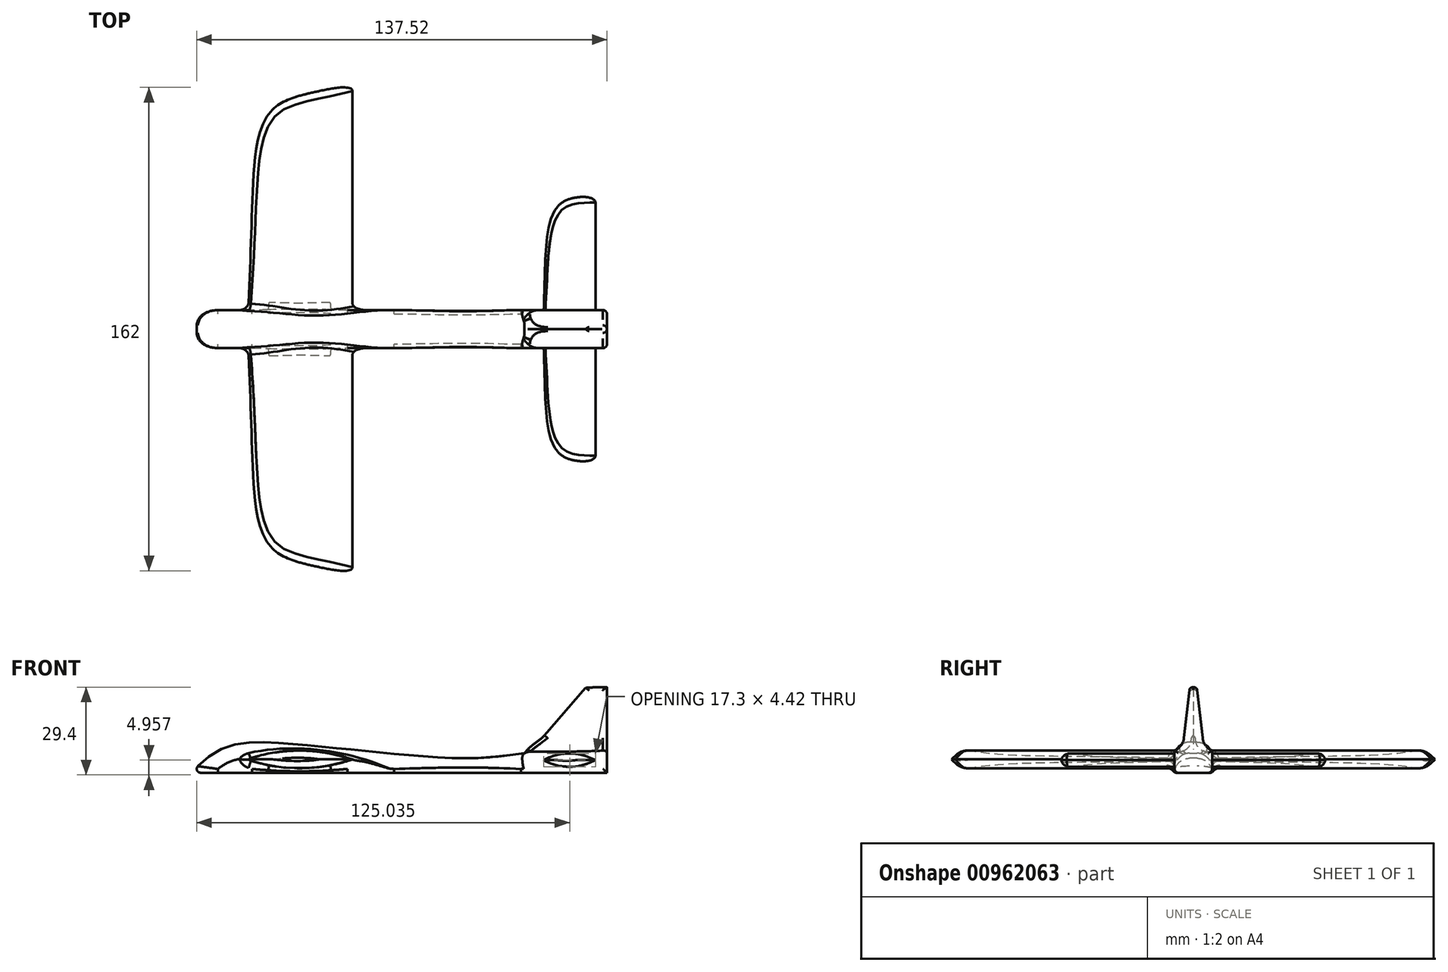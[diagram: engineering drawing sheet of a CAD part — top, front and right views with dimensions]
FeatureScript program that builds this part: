
annotation { "Feature Type Name" : "Feature", "Feature Type Description" : "" }
export const myFeature = defineFeature(function(context is Context, id is Id, definition is map)
    precondition{}
    {
        {
            var Q0;
            Q0=qCreatedBy(makeId("Front.planeOp"),FACE);
            var sketch = newSketch(context, id + "F0", { "sketchPlane" : qUnion([Q0])});
            skFitSpline(sketch, "E0", {"points": [v(-74.02, 0) * mm, v(-62.04, 8.76) * mm, v(-38.25, 9.5) * mm, v(-3.96, 6.18) * mm, v(20.19, 4.89) * mm, v(37.7, 6.54) * mm], "startDerivative": vector(65.47, 64.78) * mm, "endDerivative": vector(96.26, 12.74) * mm});
            skLineSegment(sketch, "E1", {"start": v(37.7, 6.54) * mm, "end": v(56.87, 28.67) * mm});
            skLineSegment(sketch, "E2", {"start": v(56.87, 28.67) * mm, "end": v(65.35, 28.67) * mm});
            skLineSegment(sketch, "E3", {"start": v(65.35, 28.67) * mm, "end": v(65.35, 6.54) * mm});
            skLineSegment(sketch, "E4", {"start": v(65.35, 6.54) * mm, "end": v(65.35, 0) * mm});
            skLineSegment(sketch, "E5", {"start": v(65.35, 0) * mm, "end": v(-74.02, 0) * mm});
            skSolve(sketch);
        }
        {
            var Q0;
            Q0 = qSketchRegion(id + "F0", true);
            extrude(context, id + "F1", {"entities" : qUnion([Q0]), "endBound" : BoundingType.SYMMETRIC, "depth" : 12.7 * mm, "offsetDistance" : 25.4 * mm});
        }
        {
            var Q0;
            Q0=makeQuery(id+"F1.opExtrude","CAP_FACE",FACE,{"disambiguationData":[OSD([sQuery(id+"F0.wireOp",EDGE,"E0"),sQuery(id+"F0.wireOp",EDGE,"E1"),sQuery(id+"F0.wireOp",EDGE,"E2"),sQuery(id+"F0.wireOp",EDGE,"E3"),sQuery(id+"F0.wireOp",EDGE,"E4"),sQuery(id+"F0.wireOp",EDGE,"E5")])],"isStart":false});
            var sketch = newSketch(context, id + "F2", { "sketchPlane" : qUnion([Q0])});
            skArc(sketch, "E6", {"start": v(-20.01, 4.47) * mm, "mid": v(-37.66, 7.42) * mm, "end": v(-55.32, 4.47) * mm});
            skLineSegment(sketch, "E7", {"start": v(-55.32, 4.47) * mm, "end": v(-20.01, 4.47) * mm, "construction": true});
            skArc(sketch, "E8.MirrorCS", {"start": v(-20.01, 4.47) * mm, "mid": v(-37.66, 1.52) * mm, "end": v(-55.32, 4.47) * mm});
            skSolve(sketch);
        }
        {
            var Q0;
            Q0 = qSketchRegion(id + "F2", true);
            extrude(context, id + "F3", {"entities" : qUnion([Q0]), "operationType" : NewBodyOperationType.ADD, "depth" : 76.2 * mm, "offsetDistance" : 25.4 * mm});
        }
        {
            var Q0;
            Q0=qCreatedBy(makeId("Top.planeOp"),FACE);
            var sketch = newSketch(context, id + "F4", { "sketchPlane" : qUnion([Q0])});
            skLineSegment(sketch, "E9.0", {"start": v(-20.01, -82.55) * mm, "end": v(-55.32, -82.55) * mm});
            skLineSegment(sketch, "E10.0", {"start": v(-55.32, -82.55) * mm, "end": v(-55.32, -14.48) * mm});
            skFitSpline(sketch, "E11", {"points": [v(-20.01, -82.55) * mm, v(-47.38, -72.94) * mm, v(-55.32, -14.48) * mm], "startDerivative": vector(-85.68, 26.93) * mm, "endDerivative": vector(-10.24, 146.64) * mm});
            skPoint(sketch, "E12.1.internal.snap0", {"position": v(-55.32, -44.45) * mm});
            skPoint(sketch, "E13.orphan", {"position": v(-55.32, -6.35) * mm});
            skSolve(sketch);
        }
        {
            var Q0;
            Q0 = qSketchRegion(id + "F4", true);
            extrude(context, id + "F5", {"entities" : qUnion([Q0]), "operationType" : NewBodyOperationType.REMOVE, "endBound" : BoundingType.THROUGH_ALL, "depth" : 25.4 * mm, "offsetDistance" : 25.4 * mm});
        }
        {
            var Q0;
            Q0=makeQuery(id+"F1.opExtrude","CAP_FACE",FACE,{"disambiguationData":[OSD([sQuery(id+"F0.wireOp",EDGE,"E0"),sQuery(id+"F0.wireOp",EDGE,"E1"),sQuery(id+"F0.wireOp",EDGE,"E2"),sQuery(id+"F0.wireOp",EDGE,"E3"),sQuery(id+"F0.wireOp",EDGE,"E4"),sQuery(id+"F0.wireOp",EDGE,"E5")])],"isStart":false});
            var sketch = newSketch(context, id + "F6", { "sketchPlane" : qUnion([Q0])});
            skArc(sketch, "E14", {"start": v(61.51, 4.23) * mm, "mid": v(52.77, 6.44) * mm, "end": v(44.04, 4.23) * mm});
            skLineSegment(sketch, "E15", {"start": v(44.04, 4.23) * mm, "end": v(61.51, 4.23) * mm, "construction": true});
            skArc(sketch, "E16.MirrorCS", {"start": v(61.51, 4.23) * mm, "mid": v(52.77, 2.01) * mm, "end": v(44.04, 4.23) * mm});
            skSolve(sketch);
        }
        {
            var Q0;
            Q0 = qSketchRegion(id + "F6", true);
            extrude(context, id + "F7", {"entities" : qUnion([Q0]), "operationType" : NewBodyOperationType.ADD, "depth" : 38.1 * mm, "offsetDistance" : 25.4 * mm});
        }
        {
            var Q0;
            Q0=qCreatedBy(makeId("Top.planeOp"),FACE);
            var sketch = newSketch(context, id + "F8", { "sketchPlane" : qUnion([Q0])});
            skLineSegment(sketch, "E17.0", {"start": v(61.51, -44.45) * mm, "end": v(44.04, -44.45) * mm});
            skLineSegment(sketch, "E18.0", {"start": v(44.04, -44.45) * mm, "end": v(44.04, -16.43) * mm});
            skFitSpline(sketch, "E19", {"points": [v(61.51, -44.45) * mm, v(49.07, -41.34) * mm, v(44.04, -16.43) * mm], "startDerivative": vector(-34.4, 0.2) * mm, "endDerivative": vector(-2.36, 52.88) * mm});
            skPoint(sketch, "E20.orphan", {"position": v(44.04, -6.35) * mm});
            skSolve(sketch);
        }
        {
            var Q0;
            Q0 = qSketchRegion(id + "F8", true);
            extrude(context, id + "F9", {"entities" : qUnion([Q0]), "operationType" : NewBodyOperationType.REMOVE, "endBound" : BoundingType.THROUGH_ALL, "depth" : 25.4 * mm, "offsetDistance" : 25.4 * mm});
        }
        {
            var Q0;
            Q0=makeQuery(id+"F1.opExtrude","SWEPT_BODY",BODY,{"disambiguationData":[OSD([sQuery(id+"F0.wireOp",EDGE,"E0"),sQuery(id+"F0.wireOp",EDGE,"E1"),sQuery(id+"F0.wireOp",EDGE,"E2"),sQuery(id+"F0.wireOp",EDGE,"E3"),sQuery(id+"F0.wireOp",EDGE,"E4"),sQuery(id+"F0.wireOp",EDGE,"E5")])]});
            var Q1;
            Q1=qCreatedBy(makeId("Front.planeOp"),FACE);
            mirror(context, id + "F10", {"operationType" : NewBodyOperationType.ADD, "entities" : qUnion([Q0]), "mirrorPlane" : qUnion([Q1])});
        }
        {
            var Q0;
            Q0=makeQuery(id+"F1.opExtrude","CAP_EDGE",EDGE,{"disambiguationData":[OSD([sQuery(id+"F0.wireOp",EDGE,"E0")])],"isStart":false});
            var Q1;
            Q1=makeQuery(id+"F1.opExtrude","CAP_EDGE",EDGE,{"disambiguationData":[OSD([sQuery(id+"F0.wireOp",EDGE,"E0")])],"isStart":true});
            fillet(context, id + "F11", {"entities" : qUnion([Q0, Q1]), "radius" : 5.08 * mm, "tangentPropagation" : true, "allowEdgeOverflow" : false});
        }
        {
            var Q0;
            Q0=makeQuery(id+"F10.opPattern","COPY",EDGE,{"derivedFrom":makeQuery(id+"F5.boolean.opBoolean","INTERSECT",EDGE,{"derivedFrom":[makeQuery(id+"F3.opExtrude","SWEPT_FACE",FACE,{"disambiguationData":[OSD([sQuery(id+"F2.wireOp",EDGE,"E6")])]}),makeQuery(id+"F5.opExtrude","SWEPT_FACE",FACE,{"disambiguationData":[OSD([sQuery(id+"F4.wireOp",EDGE,"E11")])]})]}),"instanceName":"1"});
            var Q1;
            Q1=makeQuery(id+"F10.opPattern","COPY",EDGE,{"derivedFrom":makeQuery(id+"F5.boolean.opBoolean","INTERSECT",EDGE,{"derivedFrom":[makeQuery(id+"F3.opExtrude","SWEPT_FACE",FACE,{"disambiguationData":[OSD([sQuery(id+"F2.wireOp",EDGE,"E8.MirrorCS")])]}),makeQuery(id+"F5.opExtrude","SWEPT_FACE",FACE,{"disambiguationData":[OSD([sQuery(id+"F4.wireOp",EDGE,"E11")])]})]}),"instanceName":"1"});
            var Q2;
            Q2=makeQuery(id+"F5.boolean.opBoolean","INTERSECT",EDGE,{"derivedFrom":[makeQuery(id+"F3.opExtrude","SWEPT_FACE",FACE,{"disambiguationData":[OSD([sQuery(id+"F2.wireOp",EDGE,"E8.MirrorCS")])]}),makeQuery(id+"F5.opExtrude","SWEPT_FACE",FACE,{"disambiguationData":[OSD([sQuery(id+"F4.wireOp",EDGE,"E11")])]})]});
            var Q3;
            Q3=makeQuery(id+"F5.boolean.opBoolean","INTERSECT",EDGE,{"derivedFrom":[makeQuery(id+"F3.opExtrude","SWEPT_FACE",FACE,{"disambiguationData":[OSD([sQuery(id+"F2.wireOp",EDGE,"E6")])]}),makeQuery(id+"F5.opExtrude","SWEPT_FACE",FACE,{"disambiguationData":[OSD([sQuery(id+"F4.wireOp",EDGE,"E11")])]})]});
            fillet(context, id + "F12", {"entities" : qUnion([Q0, Q1, Q2, Q3]), "radius" : 2.41 * mm, "tangentPropagation" : true, "allowEdgeOverflow" : false});
        }
        {
            var Q0;
            Q0=makeQuery(id+"F10.opPattern","COPY",EDGE,{"derivedFrom":makeQuery(id+"F9.boolean.opBoolean","INTERSECT",EDGE,{"derivedFrom":[makeQuery(id+"F7.opExtrude","SWEPT_FACE",FACE,{"disambiguationData":[OSD([sQuery(id+"F6.wireOp",EDGE,"E14")])]}),makeQuery(id+"F9.opExtrude","SWEPT_FACE",FACE,{"disambiguationData":[OSD([sQuery(id+"F8.wireOp",EDGE,"E19")])]})]}),"instanceName":"1"});
            var Q1;
            Q1=makeQuery(id+"F10.opPattern","COPY",EDGE,{"derivedFrom":makeQuery(id+"F9.boolean.opBoolean","INTERSECT",EDGE,{"derivedFrom":[makeQuery(id+"F7.opExtrude","SWEPT_FACE",FACE,{"disambiguationData":[OSD([sQuery(id+"F6.wireOp",EDGE,"E16.MirrorCS")])]}),makeQuery(id+"F9.opExtrude","SWEPT_FACE",FACE,{"disambiguationData":[OSD([sQuery(id+"F8.wireOp",EDGE,"E19")])]})]}),"instanceName":"1"});
            var Q2;
            Q2=makeQuery(id+"F9.boolean.opBoolean","INTERSECT",EDGE,{"derivedFrom":[makeQuery(id+"F7.opExtrude","SWEPT_FACE",FACE,{"disambiguationData":[OSD([sQuery(id+"F6.wireOp",EDGE,"E16.MirrorCS")])]}),makeQuery(id+"F9.opExtrude","SWEPT_FACE",FACE,{"disambiguationData":[OSD([sQuery(id+"F8.wireOp",EDGE,"E19")])]})]});
            var Q3;
            Q3=makeQuery(id+"F9.boolean.opBoolean","INTERSECT",EDGE,{"derivedFrom":[makeQuery(id+"F7.opExtrude","SWEPT_FACE",FACE,{"disambiguationData":[OSD([sQuery(id+"F6.wireOp",EDGE,"E14")])]}),makeQuery(id+"F9.opExtrude","SWEPT_FACE",FACE,{"disambiguationData":[OSD([sQuery(id+"F8.wireOp",EDGE,"E19")])]})]});
            fillet(context, id + "F13", {"entities" : qUnion([Q0, Q1, Q2, Q3]), "radius" : 2.03 * mm, "tangentPropagation" : true, "allowEdgeOverflow" : false});
        }
        {
            var Q0;
            Q0=makeQuery(id+"F1.opExtrude","SWEPT_FACE",FACE,{"disambiguationData":[OSD([sQuery(id+"F0.wireOp",EDGE,"E2")])]});
            var sketch = newSketch(context, id + "F14", { "sketchPlane" : qUnion([Q0])});
            skLineSegment(sketch, "E21.bottom", {"start": v(37.78, -3.81) * mm, "end": v(67.1, -3.81) * mm});
            skLineSegment(sketch, "E21.top", {"start": v(37.78, 3.81) * mm, "end": v(67.1, 3.81) * mm});
            skLineSegment(sketch, "E21.left", {"start": v(37.78, -3.81) * mm, "end": v(37.78, 3.81) * mm});
            skLineSegment(sketch, "E21.right", {"start": v(67.1, -3.81) * mm, "end": v(67.1, 3.81) * mm});
            skLineSegment(sketch, "E22.bottom", {"start": v(33.91, -6.35) * mm, "end": v(71.8, -6.35) * mm});
            skLineSegment(sketch, "E22.top", {"start": v(33.91, 6.35) * mm, "end": v(71.8, 6.35) * mm});
            skLineSegment(sketch, "E22.left", {"start": v(33.91, -6.35) * mm, "end": v(33.91, 6.35) * mm});
            skLineSegment(sketch, "E22.right", {"start": v(71.8, -6.35) * mm, "end": v(71.8, 6.35) * mm});
            skSolve(sketch);
        }
        {
            var Q0;
            Q0 = qSketchRegion(id + "F14", true);
            extrude(context, id + "F15", {"entities" : qUnion([Q0]), "operationType" : NewBodyOperationType.REMOVE, "oppositeDirection" : true, "depth" : 21.59 * mm, "offsetDistance" : 25.4 * mm});
        }
        {
            var Q0;
            Q0=makeQuery(id+"F15.boolean.opBoolean","INTERSECT",EDGE,{"derivedFrom":[makeQuery(id+"F1.opExtrude","SWEPT_FACE",FACE,{"disambiguationData":[OSD([sQuery(id+"F0.wireOp",EDGE,"E1")])]}),makeQuery(id+"F15.opExtrude","SWEPT_FACE",FACE,{"disambiguationData":[OSD([sQuery(id+"F14.wireOp",EDGE,"E21.bottom")])]})]});
            var Q1;
            Q1=makeQuery(id+"F15.boolean.opBoolean","INTERSECT",EDGE,{"derivedFrom":[makeQuery(id+"F1.opExtrude","SWEPT_FACE",FACE,{"disambiguationData":[OSD([sQuery(id+"F0.wireOp",EDGE,"E1")])]}),makeQuery(id+"F15.opExtrude","SWEPT_FACE",FACE,{"disambiguationData":[OSD([sQuery(id+"F14.wireOp",EDGE,"E21.top")])]})]});
            chamfer(context, id + "F16", {"entities" : qUnion([Q0, Q1]), "chamferType" : ChamferType.OFFSET_ANGLE, "width" : 20.32 * mm, "oppositeDirection" : true, "angle" : 10 * degree, "tangentPropagation" : true});
        }
        {
            var Q0;
            {var subQ2=sQuery(id+"F0.wireOp",EDGE,"E1");var subQ3=makeQuery(id+"F1.opExtrude","SWEPT_FACE",FACE,{"disambiguationData":[OSD([subQ2])]});var subQ4=sQuery(id+"F14.wireOp",EDGE,"E21.top");var subQ5=makeQuery(id+"F15.opExtrude","SWEPT_FACE",FACE,{"disambiguationData":[OSD([subQ4])]});Q0=makeQuery(id+"F16.opChamfer","BLEND_EDGE",EDGE,{"blendedFrom":[makeQuery(id+"F15.boolean.opBoolean","INTERSECT",EDGE,{"derivedFrom":[subQ3,subQ5]}),makeQuery(id+"F15.boolean.opBoolean","COPY",FACE,{"disambiguationData":[TD([subQ5])],"derivedFrom":makeQuery(id+"F15.opExtrude","CAP_FACE",FACE,{"disambiguationData":[OSD([sQuery(id+"F14.wireOp",EDGE,"E21.bottom"),subQ4,sQuery(id+"F14.wireOp",EDGE,"E21.left"),sQuery(id+"F14.wireOp",EDGE,"E21.right"),sQuery(id+"F14.wireOp",EDGE,"E22.bottom"),sQuery(id+"F14.wireOp",EDGE,"E22.top"),sQuery(id+"F14.wireOp",EDGE,"E22.left"),sQuery(id+"F14.wireOp",EDGE,"E22.right")])],"isStart":false})})],"blendedInto":[makeQuery(id+"F15.boolean.opBoolean","COPY",FACE,{"disambiguationData":[TD([subQ5])],"derivedFrom":makeQuery(id+"F15.opExtrude","CAP_FACE",FACE,{"disambiguationData":[OSD([sQuery(id+"F14.wireOp",EDGE,"E21.bottom"),subQ4,sQuery(id+"F14.wireOp",EDGE,"E21.left"),sQuery(id+"F14.wireOp",EDGE,"E21.right"),sQuery(id+"F14.wireOp",EDGE,"E22.bottom"),sQuery(id+"F14.wireOp",EDGE,"E22.top"),sQuery(id+"F14.wireOp",EDGE,"E22.left"),sQuery(id+"F14.wireOp",EDGE,"E22.right")])],"isStart":false})})]});}
            var Q1;
            {var subQ2=sQuery(id+"F0.wireOp",EDGE,"E1");var subQ3=makeQuery(id+"F1.opExtrude","SWEPT_FACE",FACE,{"disambiguationData":[OSD([subQ2])]});var subQ4=sQuery(id+"F14.wireOp",EDGE,"E21.bottom");var subQ5=makeQuery(id+"F15.opExtrude","SWEPT_FACE",FACE,{"disambiguationData":[OSD([subQ4])]});Q1=makeQuery(id+"F16.opChamfer","BLEND_EDGE",EDGE,{"blendedFrom":[makeQuery(id+"F15.boolean.opBoolean","INTERSECT",EDGE,{"derivedFrom":[subQ3,subQ5]}),makeQuery(id+"F15.boolean.opBoolean","COPY",FACE,{"disambiguationData":[TD([subQ5])],"derivedFrom":makeQuery(id+"F15.opExtrude","CAP_FACE",FACE,{"disambiguationData":[OSD([subQ4,sQuery(id+"F14.wireOp",EDGE,"E21.top"),sQuery(id+"F14.wireOp",EDGE,"E21.left"),sQuery(id+"F14.wireOp",EDGE,"E21.right"),sQuery(id+"F14.wireOp",EDGE,"E22.bottom"),sQuery(id+"F14.wireOp",EDGE,"E22.top"),sQuery(id+"F14.wireOp",EDGE,"E22.left"),sQuery(id+"F14.wireOp",EDGE,"E22.right")])],"isStart":false})})],"blendedInto":[makeQuery(id+"F15.boolean.opBoolean","COPY",FACE,{"disambiguationData":[TD([subQ5])],"derivedFrom":makeQuery(id+"F15.opExtrude","CAP_FACE",FACE,{"disambiguationData":[OSD([subQ4,sQuery(id+"F14.wireOp",EDGE,"E21.top"),sQuery(id+"F14.wireOp",EDGE,"E21.left"),sQuery(id+"F14.wireOp",EDGE,"E21.right"),sQuery(id+"F14.wireOp",EDGE,"E22.bottom"),sQuery(id+"F14.wireOp",EDGE,"E22.top"),sQuery(id+"F14.wireOp",EDGE,"E22.left"),sQuery(id+"F14.wireOp",EDGE,"E22.right")])],"isStart":false})})]});}
            fillet(context, id + "F17", {"entities" : qUnion([Q0, Q1]), "radius" : 5.08 * mm, "tangentPropagation" : true, "allowEdgeOverflow" : false});
        }
        {
            var Q0;
            Q0=makeQuery(id+"F10.opPattern","COPY",EDGE,{"derivedFrom":makeQuery(id+"F7.opExtrude","CAP_EDGE",EDGE,{"disambiguationData":[OSD([sQuery(id+"F6.wireOp",EDGE,"E14")])],"isStart":true}),"instanceName":"1"});
            var Q1;
            Q1=makeQuery(id+"F10.opPattern","COPY",EDGE,{"derivedFrom":makeQuery(id+"F7.opExtrude","CAP_EDGE",EDGE,{"disambiguationData":[OSD([sQuery(id+"F6.wireOp",EDGE,"E16.MirrorCS")])],"isStart":true}),"instanceName":"1"});
            var Q2;
            Q2=makeQuery(id+"F7.opExtrude","CAP_EDGE",EDGE,{"disambiguationData":[OSD([sQuery(id+"F6.wireOp",EDGE,"E14")])],"isStart":true});
            var Q3;
            Q3=makeQuery(id+"F7.opExtrude","CAP_EDGE",EDGE,{"disambiguationData":[OSD([sQuery(id+"F6.wireOp",EDGE,"E16.MirrorCS")])],"isStart":true});
            var Q4;
            Q4=makeQuery(id+"F11.opFillet","BLEND_EDGE",EDGE,{"blendedFrom":[makeQuery(id+"F1.opExtrude","CAP_EDGE",EDGE,{"disambiguationData":[OSD([sQuery(id+"F0.wireOp",EDGE,"E0")])],"isStart":false}),makeQuery(id+"F3.opExtrude","SWEPT_FACE",FACE,{"disambiguationData":[OSD([sQuery(id+"F2.wireOp",EDGE,"E6")])]})],"blendedInto":[makeQuery(id+"F3.opExtrude","SWEPT_FACE",FACE,{"disambiguationData":[OSD([sQuery(id+"F2.wireOp",EDGE,"E6")])]})]});
            var Q5;
            Q5=makeQuery(id+"F11.opFillet","BLEND_EDGE",EDGE,{"blendedFrom":[makeQuery(id+"F1.opExtrude","CAP_EDGE",EDGE,{"disambiguationData":[OSD([sQuery(id+"F0.wireOp",EDGE,"E0")])],"isStart":false}),makeQuery(id+"F3.opExtrude","SWEPT_FACE",FACE,{"disambiguationData":[OSD([sQuery(id+"F2.wireOp",EDGE,"E8.MirrorCS")])]})],"blendedInto":[makeQuery(id+"F3.opExtrude","SWEPT_FACE",FACE,{"disambiguationData":[OSD([sQuery(id+"F2.wireOp",EDGE,"E8.MirrorCS")])]})]});
            var Q6;
            Q6=makeQuery(id+"F11.opFillet","BLEND_EDGE",EDGE,{"blendedFrom":[makeQuery(id+"F1.opExtrude","CAP_EDGE",EDGE,{"disambiguationData":[OSD([sQuery(id+"F0.wireOp",EDGE,"E0")])],"isStart":true}),makeQuery(id+"F10.opPattern","COPY",FACE,{"derivedFrom":makeQuery(id+"F3.opExtrude","SWEPT_FACE",FACE,{"disambiguationData":[OSD([sQuery(id+"F2.wireOp",EDGE,"E6")])]}),"instanceName":"1"})],"blendedInto":[makeQuery(id+"F10.opPattern","COPY",FACE,{"derivedFrom":makeQuery(id+"F3.opExtrude","SWEPT_FACE",FACE,{"disambiguationData":[OSD([sQuery(id+"F2.wireOp",EDGE,"E6")])]}),"instanceName":"1"})]});
            var Q7;
            Q7=makeQuery(id+"F11.opFillet","BLEND_EDGE",EDGE,{"blendedFrom":[makeQuery(id+"F1.opExtrude","CAP_EDGE",EDGE,{"disambiguationData":[OSD([sQuery(id+"F0.wireOp",EDGE,"E0")])],"isStart":true}),makeQuery(id+"F10.opPattern","COPY",FACE,{"derivedFrom":makeQuery(id+"F3.opExtrude","SWEPT_FACE",FACE,{"disambiguationData":[OSD([sQuery(id+"F2.wireOp",EDGE,"E8.MirrorCS")])]}),"instanceName":"1"})],"blendedInto":[makeQuery(id+"F10.opPattern","COPY",FACE,{"derivedFrom":makeQuery(id+"F3.opExtrude","SWEPT_FACE",FACE,{"disambiguationData":[OSD([sQuery(id+"F2.wireOp",EDGE,"E8.MirrorCS")])]}),"instanceName":"1"})]});
            fillet(context, id + "F18", {"entities" : qUnion([Q0, Q1, Q2, Q3, Q4, Q5, Q6, Q7]), "radius" : 2.54 * mm, "tangentPropagation" : true, "allowEdgeOverflow" : false});
        }
        {
            var Q0;
            Q0=makeQuery(id+"F1.opExtrude","CAP_EDGE",EDGE,{"disambiguationData":[OSD([sQuery(id+"F0.wireOp",EDGE,"E1")])],"isStart":false});
            var Q1;
            Q1=makeQuery(id+"F1.opExtrude","CAP_EDGE",EDGE,{"disambiguationData":[OSD([sQuery(id+"F0.wireOp",EDGE,"E1")])],"isStart":true});
            var Q2;
            {var subQ0=sQuery(id+"F0.wireOp",EDGE,"E1");var subQ1=makeQuery(id+"F1.opExtrude","SWEPT_FACE",FACE,{"disambiguationData":[OSD([subQ0])]});var subQ2=subQ1;var subQ5=sQuery(id+"F14.wireOp",EDGE,"E21.top");var subQ6=makeQuery(id+"F15.opExtrude","SWEPT_FACE",FACE,{"disambiguationData":[OSD([subQ5])]});Q2=makeQuery(id+"F17.opFillet","BLEND_EDGE",EDGE,{"blendedFrom":[makeQuery(id+"F16.opChamfer","BLEND_EDGE",EDGE,{"blendedFrom":[makeQuery(id+"F15.boolean.opBoolean","INTERSECT",EDGE,{"derivedFrom":[subQ2,subQ6]}),makeQuery(id+"F15.boolean.opBoolean","COPY",FACE,{"disambiguationData":[TD([subQ6])],"derivedFrom":makeQuery(id+"F15.opExtrude","CAP_FACE",FACE,{"disambiguationData":[OSD([sQuery(id+"F14.wireOp",EDGE,"E21.bottom"),subQ5,sQuery(id+"F14.wireOp",EDGE,"E21.left"),sQuery(id+"F14.wireOp",EDGE,"E21.right"),sQuery(id+"F14.wireOp",EDGE,"E22.bottom"),sQuery(id+"F14.wireOp",EDGE,"E22.top"),sQuery(id+"F14.wireOp",EDGE,"E22.left"),sQuery(id+"F14.wireOp",EDGE,"E22.right")])],"isStart":false})})],"blendedInto":[makeQuery(id+"F15.boolean.opBoolean","COPY",FACE,{"disambiguationData":[TD([subQ6])],"derivedFrom":makeQuery(id+"F15.opExtrude","CAP_FACE",FACE,{"disambiguationData":[OSD([sQuery(id+"F14.wireOp",EDGE,"E21.bottom"),subQ5,sQuery(id+"F14.wireOp",EDGE,"E21.left"),sQuery(id+"F14.wireOp",EDGE,"E21.right"),sQuery(id+"F14.wireOp",EDGE,"E22.bottom"),sQuery(id+"F14.wireOp",EDGE,"E22.top"),sQuery(id+"F14.wireOp",EDGE,"E22.left"),sQuery(id+"F14.wireOp",EDGE,"E22.right")])],"isStart":false})})]}),subQ2],"blendedInto":[subQ2]});}
            var Q3;
            {var subQ0=sQuery(id+"F0.wireOp",EDGE,"E1");var subQ1=makeQuery(id+"F1.opExtrude","SWEPT_FACE",FACE,{"disambiguationData":[OSD([subQ0])]});var subQ2=subQ1;var subQ5=sQuery(id+"F14.wireOp",EDGE,"E21.bottom");var subQ6=makeQuery(id+"F15.opExtrude","SWEPT_FACE",FACE,{"disambiguationData":[OSD([subQ5])]});Q3=makeQuery(id+"F17.opFillet","BLEND_EDGE",EDGE,{"blendedFrom":[makeQuery(id+"F16.opChamfer","BLEND_EDGE",EDGE,{"blendedFrom":[makeQuery(id+"F15.boolean.opBoolean","INTERSECT",EDGE,{"derivedFrom":[subQ2,subQ6]}),makeQuery(id+"F15.boolean.opBoolean","COPY",FACE,{"disambiguationData":[TD([subQ6])],"derivedFrom":makeQuery(id+"F15.opExtrude","CAP_FACE",FACE,{"disambiguationData":[OSD([subQ5,sQuery(id+"F14.wireOp",EDGE,"E21.top"),sQuery(id+"F14.wireOp",EDGE,"E21.left"),sQuery(id+"F14.wireOp",EDGE,"E21.right"),sQuery(id+"F14.wireOp",EDGE,"E22.bottom"),sQuery(id+"F14.wireOp",EDGE,"E22.top"),sQuery(id+"F14.wireOp",EDGE,"E22.left"),sQuery(id+"F14.wireOp",EDGE,"E22.right")])],"isStart":false})})],"blendedInto":[makeQuery(id+"F15.boolean.opBoolean","COPY",FACE,{"disambiguationData":[TD([subQ6])],"derivedFrom":makeQuery(id+"F15.opExtrude","CAP_FACE",FACE,{"disambiguationData":[OSD([subQ5,sQuery(id+"F14.wireOp",EDGE,"E21.top"),sQuery(id+"F14.wireOp",EDGE,"E21.left"),sQuery(id+"F14.wireOp",EDGE,"E21.right"),sQuery(id+"F14.wireOp",EDGE,"E22.bottom"),sQuery(id+"F14.wireOp",EDGE,"E22.top"),sQuery(id+"F14.wireOp",EDGE,"E22.left"),sQuery(id+"F14.wireOp",EDGE,"E22.right")])],"isStart":false})})]}),subQ2],"blendedInto":[subQ2]});}
            fillet(context, id + "F19", {"entities" : qUnion([Q0, Q1, Q2, Q3]), "radius" : 3.17 * mm, "tangentPropagation" : true, "allowEdgeOverflow" : false});
        }
        {
            var Q0;
            Q0=makeQuery(id+"F1.opExtrude","CAP_EDGE",EDGE,{"disambiguationData":[OSD([sQuery(id+"F0.wireOp",EDGE,"E5")])],"isStart":true});
            var Q1;
            Q1=makeQuery(id+"F1.opExtrude","CAP_EDGE",EDGE,{"disambiguationData":[OSD([sQuery(id+"F0.wireOp",EDGE,"E3"),sQuery(id+"F0.wireOp",EDGE,"E4")])],"isStart":true});
            var Q2;
            Q2=makeQuery(id+"F1.opExtrude","CAP_EDGE",EDGE,{"disambiguationData":[OSD([sQuery(id+"F0.wireOp",EDGE,"E3"),sQuery(id+"F0.wireOp",EDGE,"E4")])],"isStart":false});
            var Q3;
            {var subQ0=sQuery(id+"F0.wireOp",EDGE,"E4");var subQ1=sQuery(id+"F0.wireOp",EDGE,"E3");var subQ2=makeQuery(id+"F1.opExtrude","SWEPT_FACE",FACE,{"disambiguationData":[OSD([subQ1,subQ0])]});var subQ3=sQuery(id+"F0.wireOp",EDGE,"E1");var subQ4=makeQuery(id+"F1.opExtrude","SWEPT_FACE",FACE,{"disambiguationData":[OSD([subQ3])]});var subQ5=sQuery(id+"F14.wireOp",EDGE,"E21.bottom");var subQ6=makeQuery(id+"F15.opExtrude","SWEPT_FACE",FACE,{"disambiguationData":[OSD([subQ5])]});Q3=makeQuery(id+"F17.opFillet","BLEND_EDGE",EDGE,{"blendedFrom":[makeQuery(id+"F16.opChamfer","BLEND_EDGE",EDGE,{"blendedFrom":[makeQuery(id+"F15.boolean.opBoolean","INTERSECT",EDGE,{"derivedFrom":[subQ4,subQ6]}),makeQuery(id+"F15.boolean.opBoolean","COPY",FACE,{"disambiguationData":[TD([subQ6])],"derivedFrom":makeQuery(id+"F15.opExtrude","CAP_FACE",FACE,{"disambiguationData":[OSD([subQ5,sQuery(id+"F14.wireOp",EDGE,"E21.top"),sQuery(id+"F14.wireOp",EDGE,"E21.left"),sQuery(id+"F14.wireOp",EDGE,"E21.right"),sQuery(id+"F14.wireOp",EDGE,"E22.bottom"),sQuery(id+"F14.wireOp",EDGE,"E22.top"),sQuery(id+"F14.wireOp",EDGE,"E22.left"),sQuery(id+"F14.wireOp",EDGE,"E22.right")])],"isStart":false})})],"blendedInto":[makeQuery(id+"F15.boolean.opBoolean","COPY",FACE,{"disambiguationData":[TD([subQ6])],"derivedFrom":makeQuery(id+"F15.opExtrude","CAP_FACE",FACE,{"disambiguationData":[OSD([subQ5,sQuery(id+"F14.wireOp",EDGE,"E21.top"),sQuery(id+"F14.wireOp",EDGE,"E21.left"),sQuery(id+"F14.wireOp",EDGE,"E21.right"),sQuery(id+"F14.wireOp",EDGE,"E22.bottom"),sQuery(id+"F14.wireOp",EDGE,"E22.top"),sQuery(id+"F14.wireOp",EDGE,"E22.left"),sQuery(id+"F14.wireOp",EDGE,"E22.right")])],"isStart":false})})]}),subQ2],"blendedInto":[subQ2]});}
            var Q4;
            {var subQ0=sQuery(id+"F0.wireOp",EDGE,"E4");var subQ1=sQuery(id+"F0.wireOp",EDGE,"E3");var subQ2=makeQuery(id+"F1.opExtrude","SWEPT_FACE",FACE,{"disambiguationData":[OSD([subQ1,subQ0])]});var subQ3=sQuery(id+"F0.wireOp",EDGE,"E1");var subQ4=makeQuery(id+"F1.opExtrude","SWEPT_FACE",FACE,{"disambiguationData":[OSD([subQ3])]});var subQ5=sQuery(id+"F14.wireOp",EDGE,"E21.top");var subQ6=makeQuery(id+"F15.opExtrude","SWEPT_FACE",FACE,{"disambiguationData":[OSD([subQ5])]});Q4=makeQuery(id+"F17.opFillet","BLEND_EDGE",EDGE,{"blendedFrom":[makeQuery(id+"F16.opChamfer","BLEND_EDGE",EDGE,{"blendedFrom":[makeQuery(id+"F15.boolean.opBoolean","INTERSECT",EDGE,{"derivedFrom":[subQ4,subQ6]}),makeQuery(id+"F15.boolean.opBoolean","COPY",FACE,{"disambiguationData":[TD([subQ6])],"derivedFrom":makeQuery(id+"F15.opExtrude","CAP_FACE",FACE,{"disambiguationData":[OSD([sQuery(id+"F14.wireOp",EDGE,"E21.bottom"),subQ5,sQuery(id+"F14.wireOp",EDGE,"E21.left"),sQuery(id+"F14.wireOp",EDGE,"E21.right"),sQuery(id+"F14.wireOp",EDGE,"E22.bottom"),sQuery(id+"F14.wireOp",EDGE,"E22.top"),sQuery(id+"F14.wireOp",EDGE,"E22.left"),sQuery(id+"F14.wireOp",EDGE,"E22.right")])],"isStart":false})})],"blendedInto":[makeQuery(id+"F15.boolean.opBoolean","COPY",FACE,{"disambiguationData":[TD([subQ6])],"derivedFrom":makeQuery(id+"F15.opExtrude","CAP_FACE",FACE,{"disambiguationData":[OSD([sQuery(id+"F14.wireOp",EDGE,"E21.bottom"),subQ5,sQuery(id+"F14.wireOp",EDGE,"E21.left"),sQuery(id+"F14.wireOp",EDGE,"E21.right"),sQuery(id+"F14.wireOp",EDGE,"E22.bottom"),sQuery(id+"F14.wireOp",EDGE,"E22.top"),sQuery(id+"F14.wireOp",EDGE,"E22.left"),sQuery(id+"F14.wireOp",EDGE,"E22.right")])],"isStart":false})})]}),subQ2],"blendedInto":[subQ2]});}
            var Q5;
            Q5=makeQuery(id+"F16.opChamfer","BLEND_EDGE",EDGE,{"blendedFrom":[makeQuery(id+"F15.boolean.opBoolean","INTERSECT",EDGE,{"derivedFrom":[makeQuery(id+"F1.opExtrude","SWEPT_FACE",FACE,{"disambiguationData":[OSD([sQuery(id+"F0.wireOp",EDGE,"E1")])]}),makeQuery(id+"F15.opExtrude","SWEPT_FACE",FACE,{"disambiguationData":[OSD([sQuery(id+"F14.wireOp",EDGE,"E21.bottom")])]})]}),makeQuery(id+"F1.opExtrude","SWEPT_FACE",FACE,{"disambiguationData":[OSD([sQuery(id+"F0.wireOp",EDGE,"E2")])]})],"blendedInto":[makeQuery(id+"F1.opExtrude","SWEPT_FACE",FACE,{"disambiguationData":[OSD([sQuery(id+"F0.wireOp",EDGE,"E2")])]})]});
            var Q6;
            Q6=makeQuery(id+"F16.opChamfer","BLEND_EDGE",EDGE,{"blendedFrom":[makeQuery(id+"F15.boolean.opBoolean","INTERSECT",EDGE,{"derivedFrom":[makeQuery(id+"F1.opExtrude","SWEPT_FACE",FACE,{"disambiguationData":[OSD([sQuery(id+"F0.wireOp",EDGE,"E1")])]}),makeQuery(id+"F15.opExtrude","SWEPT_FACE",FACE,{"disambiguationData":[OSD([sQuery(id+"F14.wireOp",EDGE,"E21.top")])]})]}),makeQuery(id+"F1.opExtrude","SWEPT_FACE",FACE,{"disambiguationData":[OSD([sQuery(id+"F0.wireOp",EDGE,"E2")])]})],"blendedInto":[makeQuery(id+"F1.opExtrude","SWEPT_FACE",FACE,{"disambiguationData":[OSD([sQuery(id+"F0.wireOp",EDGE,"E2")])]})]});
            fillet(context, id + "F20", {"entities" : qUnion([Q0, Q1, Q2, Q3, Q4, Q5, Q6]), "radius" : 1.27 * mm, "tangentPropagation" : true, "allowEdgeOverflow" : false});
        }
    });
